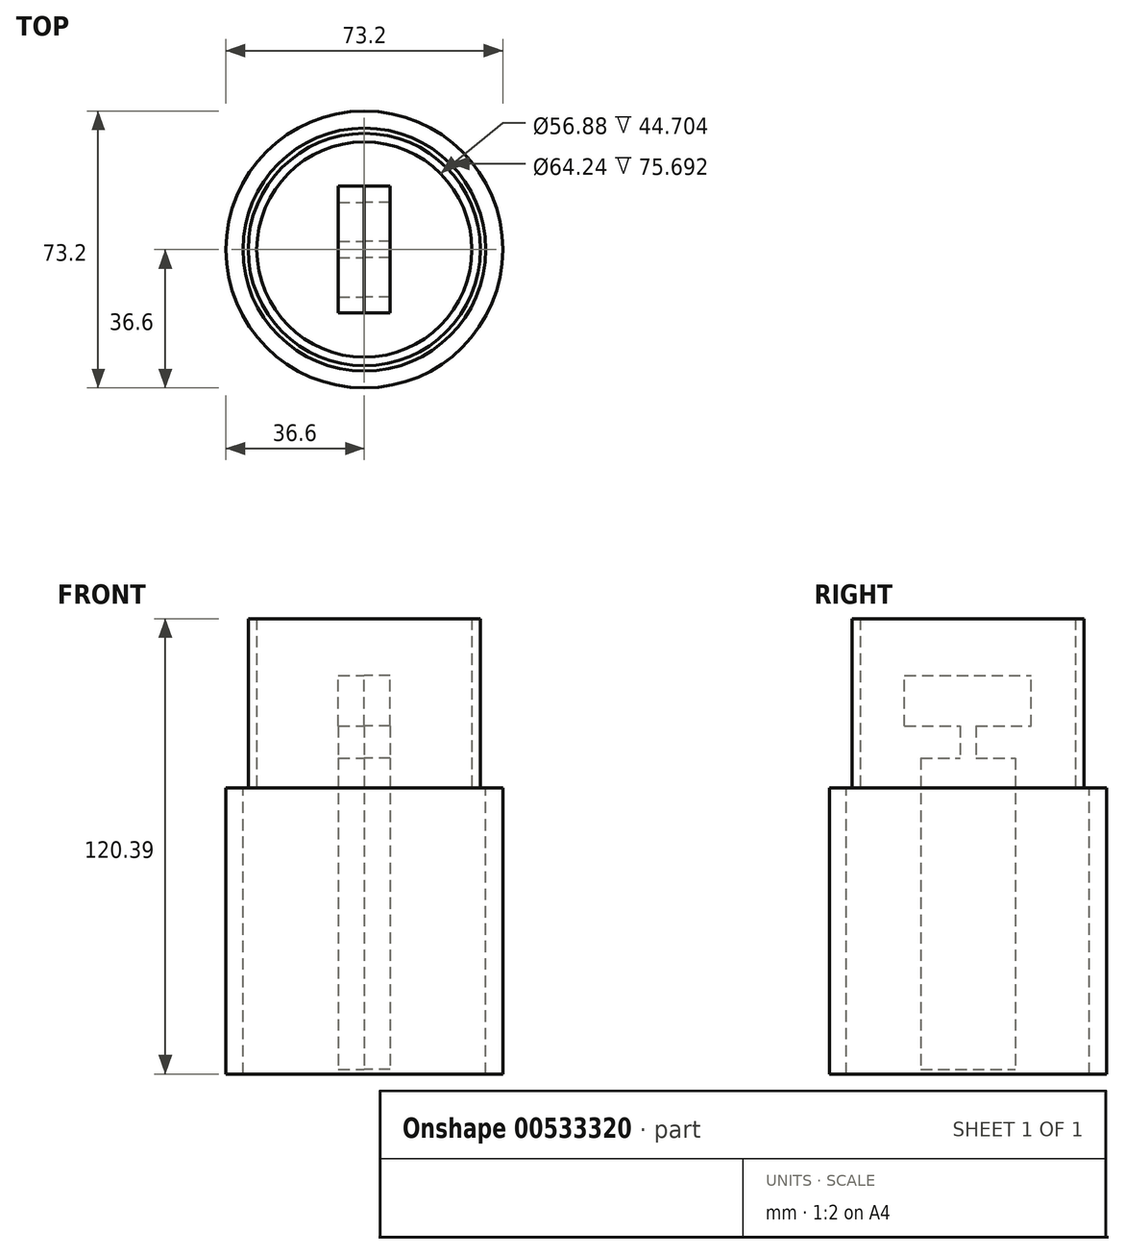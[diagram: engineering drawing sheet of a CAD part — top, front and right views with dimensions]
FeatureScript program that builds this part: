
annotation { "Feature Type Name" : "Feature", "Feature Type Description" : "" }
export const myFeature = defineFeature(function(context is Context, id is Id, definition is map)
    precondition{}
    {
        {
            var Q0;
            Q0=qCreatedBy(makeId("Top.planeOp"),FACE);
            var sketch = newSketch(context, id + "F0", { "sketchPlane" : qUnion([Q0])});
            skCircle(sketch, "E0", {"center": v(0, 0) * mm, "radius": 36.6 * mm});
            skCircle(sketch, "E1", {"center": v(0, 0) * mm, "radius": 32.12 * mm});
            skSolve(sketch);
        }
        {
            var Q0;
            Q0 = qSketchRegion(id + "F0", true);
            extrude(context, id + "F1", {"entities" : qUnion([Q0]), "oppositeDirection" : true, "depth" : 75.7 * mm, "offsetDistance" : 25.4 * mm});
        }
        {
            var Q0;
            Q0=qCreatedBy(makeId("Top.planeOp"),FACE);
            var sketch = newSketch(context, id + "F2", { "sketchPlane" : qUnion([Q0])});
            skCircle(sketch, "E2", {"center": v(0, 0) * mm, "radius": 28.44 * mm});
            skCircle(sketch, "E3", {"center": v(0, 0) * mm, "radius": 30.72 * mm});
            skSolve(sketch);
        }
        {
            var Q0;
            Q0 = qSketchRegion(id + "F2", true);
            extrude(context, id + "F3", {"entities" : qUnion([Q0]), "depth" : 44.7 * mm, "offsetDistance" : 25.4 * mm});
        }
        {
            var Q0;
            Q0=qCreatedBy(makeId("Right.planeOp"),FACE);
            var sketch = newSketch(context, id + "F4", { "sketchPlane" : qUnion([Q0])});
            skLineSegment(sketch, "E4.bottom", {"start": v(-12.5, 7.77) * mm, "end": v(12.5, 7.77) * mm});
            skLineSegment(sketch, "E4.top", {"start": v(-12.5, -74.52) * mm, "end": v(12.5, -74.52) * mm});
            skLineSegment(sketch, "E4.left", {"start": v(-12.5, 7.77) * mm, "end": v(-12.5, -74.52) * mm});
            skLineSegment(sketch, "E4.right", {"start": v(12.5, 7.77) * mm, "end": v(12.5, -74.52) * mm});
            skPoint(sketch, "E4.middle", {"position": v(0, -33.38) * mm});
            skLineSegment(sketch, "E5.bottom", {"start": v(-2.13, 16.3) * mm, "end": v(2.13, 16.3) * mm});
            skLineSegment(sketch, "E5.top", {"start": v(-2.13, -0.76) * mm, "end": v(2.13, -0.76) * mm});
            skLineSegment(sketch, "E5.left", {"start": v(-2.13, 16.3) * mm, "end": v(-2.13, -0.76) * mm});
            skLineSegment(sketch, "E5.right", {"start": v(2.13, 16.3) * mm, "end": v(2.13, -0.76) * mm});
            skPoint(sketch, "E5.middle", {"position": v(0, 7.77) * mm});
            skLineSegment(sketch, "E6.bottom", {"start": v(-16.76, 16.3) * mm, "end": v(16.76, 16.3) * mm});
            skLineSegment(sketch, "E6.top", {"start": v(-16.76, 29.72) * mm, "end": v(16.76, 29.72) * mm});
            skLineSegment(sketch, "E6.left", {"start": v(-16.76, 16.3) * mm, "end": v(-16.76, 29.72) * mm});
            skLineSegment(sketch, "E6.right", {"start": v(16.76, 16.3) * mm, "end": v(16.76, 29.72) * mm});
            skPoint(sketch, "E6.middle", {"position": v(0, 23.01) * mm});
            skSolve(sketch);
        }
        {
            var Q0;
            Q0 = qSketchRegion(id + "F4", true);
            extrude(context, id + "F5", {"entities" : qUnion([Q0]), "depth" : 6.86 * mm, "offsetDistance" : 25.4 * mm});
        }
        {
            var Q0;
            Q0=makeQuery(id+"F5.opExtrude","SWEPT_BODY",BODY,{"disambiguationData":[OSD([sQuery(id+"F4.wireOp",EDGE,"E4.bottom"),sQuery(id+"F4.wireOp",EDGE,"E4.top"),sQuery(id+"F4.wireOp",EDGE,"E4.left"),sQuery(id+"F4.wireOp",EDGE,"E4.right"),sQuery(id+"F4.wireOp",EDGE,"E5.left"),sQuery(id+"F4.wireOp",EDGE,"E5.right"),sQuery(id+"F4.wireOp",EDGE,"E6.bottom"),sQuery(id+"F4.wireOp",EDGE,"E6.top"),sQuery(id+"F4.wireOp",EDGE,"E6.left"),sQuery(id+"F4.wireOp",EDGE,"E6.right")])]});
            var Q1;
            Q1=qCreatedBy(makeId("Right.planeOp"),FACE);
            mirror(context, id + "F6", {"operationType" : NewBodyOperationType.ADD, "entities" : qUnion([Q0]), "mirrorPlane" : qUnion([Q1])});
        }
    });
